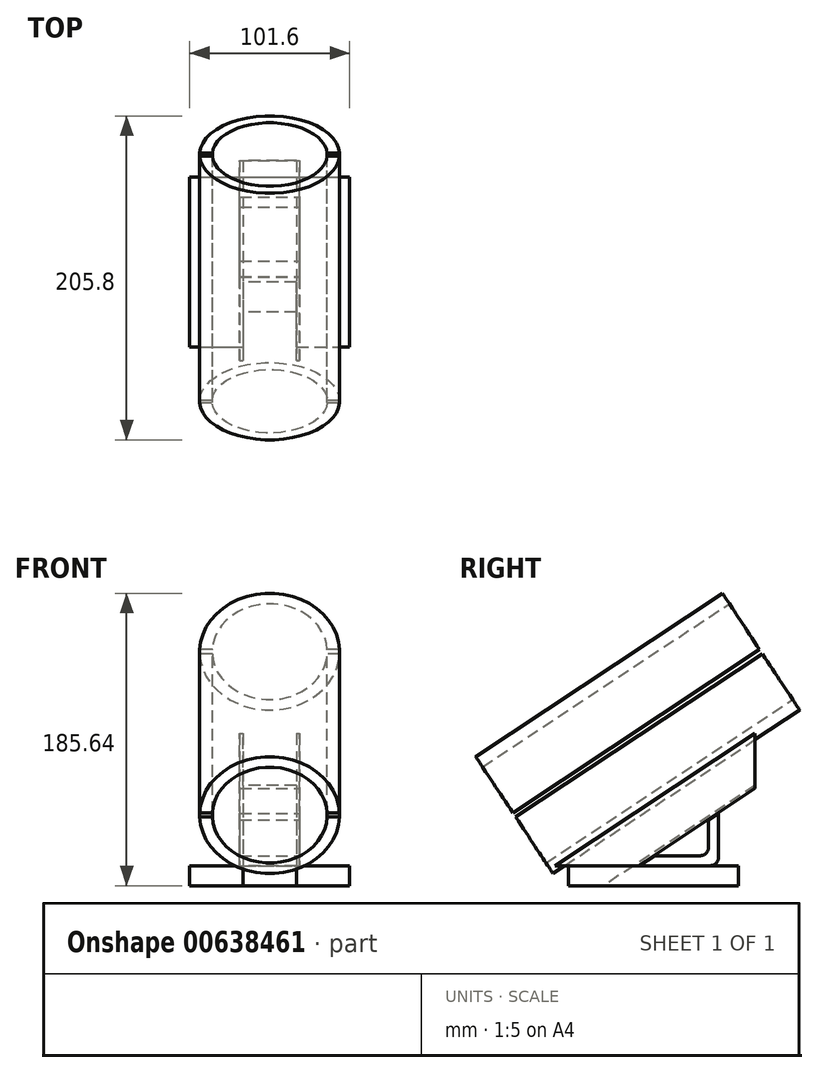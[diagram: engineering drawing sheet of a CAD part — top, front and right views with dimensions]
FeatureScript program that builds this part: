
annotation { "Feature Type Name" : "Feature", "Feature Type Description" : "" }
export const myFeature = defineFeature(function(context is Context, id is Id, definition is map)
    precondition{}
    {
        {
            var Q0;
            Q0=qCreatedBy(makeId("Top.planeOp"),FACE);
            var sketch = newSketch(context, id + "F0", { "sketchPlane" : qUnion([Q0])});
            skLineSegment(sketch, "E0.bottom", {"start": v(-50.8, 53.98) * mm, "end": v(50.8, 53.98) * mm});
            skLineSegment(sketch, "E0.top", {"start": v(-50.8, -53.98) * mm, "end": v(50.8, -53.98) * mm});
            skLineSegment(sketch, "E0.left", {"start": v(-50.8, 53.98) * mm, "end": v(-50.8, -53.98) * mm});
            skLineSegment(sketch, "E0.right", {"start": v(50.8, 53.98) * mm, "end": v(50.8, -53.98) * mm});
            skPoint(sketch, "E0.middle", {"position": v(0, 0) * mm});
            skSolve(sketch);
        }
        {
            var Q0;
            Q0 = qSketchRegion(id + "F0", true);
            extrude(context, id + "F1", {"entities" : qUnion([Q0]), "oppositeDirection" : true, "depth" : 12.7 * mm, "offsetDistance" : 25.4 * mm});
        }
        {
            var Q0;
            Q0=qCreatedBy(makeId("Right.planeOp"),FACE);
            cPlane(context, id + "F2", {"entities" : qUnion([Q0]), "cplaneType" : CPlaneType.OFFSET, "offset" : 19.05 * mm, "width" : 152.4 * mm, "height" : 152.4 * mm});
        }
        {
            var Q0;
            Q0=qCreatedBy(id+"F2.planeOp",FACE);
            var sketch = newSketch(context, id + "F3", { "sketchPlane" : qUnion([Q0])});
            skLineSegment(sketch, "E1", {"start": v(-62.56, 0) * mm, "end": v(64.53, 84.12) * mm});
            skLineSegment(sketch, "E2", {"start": v(64.53, 84.12) * mm, "end": v(64.53, 49.02) * mm});
            skLineSegment(sketch, "E3", {"start": v(64.53, 49.02) * mm, "end": v(-9.53, 0) * mm});
            skLineSegment(sketch, "E4", {"start": v(-9.52, 0) * mm, "end": v(-62.56, 0) * mm});
            skLineSegment(sketch, "E5", {"start": v(0.53, 6.35) * mm, "end": v(34.92, 6.35) * mm});
            skLineSegment(sketch, "E6", {"start": v(34.92, 6.35) * mm, "end": v(34.92, 29.12) * mm});
            skLineSegment(sketch, "E7", {"start": v(34.92, 29.42) * mm, "end": v(41.27, 33.62) * mm});
            skLineSegment(sketch, "E8", {"start": v(41.27, 33.32) * mm, "end": v(41.27, 0) * mm});
            skLineSegment(sketch, "E9", {"start": v(41.27, 0) * mm, "end": v(-9.06, 0) * mm});
            skLineSegment(sketch, "E10", {"start": v(-9.06, 0) * mm, "end": v(0.53, 6.35) * mm});
            skLineSegment(sketch, "E11", {"start": v(34.92, 29.12) * mm, "end": v(41.27, 33.32) * mm});
            skSolve(sketch);
        }
        {
            var Q0;
            Q0 = qSketchRegion(id + "F3", true);
            extrude(context, id + "F4", {"entities" : qUnion([Q0]), "oppositeDirection" : true, "depth" : 38.1 * mm, "offsetDistance" : 25.4 * mm});
        }
        {
            var Q0;
            Q0=makeQuery(id+"F4.opExtrude","SWEPT_FACE",FACE,{"disambiguationData":[OSD([sQuery(id+"F3.wireOp",EDGE,"E2")])]});
            var sketch = newSketch(context, id + "F5", { "sketchPlane" : qUnion([Q0])});
            skLineSegment(sketch, "E12", {"start": v(-17.05, 84.12) * mm, "end": v(-17.05, 51.02) * mm});
            skLineSegment(sketch, "E13", {"start": v(-17.05, 51.02) * mm, "end": v(17.05, 51.02) * mm});
            skLineSegment(sketch, "E14", {"start": v(17.05, 51.02) * mm, "end": v(17.05, 84.12) * mm});
            skLineSegment(sketch, "E15", {"start": v(17.05, 84.12) * mm, "end": v(-17.05, 84.12) * mm});
            skSolve(sketch);
        }
        {
            var Q0;
            Q0=makeQuery(id+"F5.imprint","IMPRINT",FACE,{"disambiguationData":[TD([[makeQuery(id+"F5.imprint","IMPRINT",EDGE,{"derivedFrom":sQuery(id+"F5.wireOp",EDGE,"E12")}),1.0]])]});
            var Q1;
            Q1=makeQuery(id+"F4.opExtrude","CAP_EDGE",EDGE,{"disambiguationData":[OSD([sQuery(id+"F3.wireOp",EDGE,"E1")])],"isStart":true});
            sweep(context, id + "F6", {"operationType" : NewBodyOperationType.REMOVE, "profiles" : qUnion([Q0]), "path" : qUnion([Q1])});
        }
        {
            var Q0;
            Q0=makeQuery(id+"F4.opExtrude","SWEPT_EDGE",EDGE,{"disambiguationData":[OSD([sQuery(id+"F3.wireOp",EDGE,"E8"),sQuery(id+"F3.wireOp",EDGE,"E9")])]});
            var Q1;
            Q1=makeQuery(id+"F4.opExtrude","SWEPT_EDGE",EDGE,{"disambiguationData":[OSD([sQuery(id+"F3.wireOp",EDGE,"E5"),sQuery(id+"F3.wireOp",EDGE,"E6")])]});
            fillet(context, id + "F7", {"entities" : qUnion([Q0, Q1]), "radius" : 5.08 * mm, "tangentPropagation" : true, "allowEdgeOverflow" : false});
        }
        {
            var Q0;
            {var subQ0=sQuery(id+"F3.wireOp",EDGE,"E1");var subQ1=sQuery(id+"F3.wireOp",EDGE,"E2");Q0=makeQuery(id+"F6.boolean.opBoolean","SPLIT",EDGE,{"disambiguationData":[TD([makeQuery(id+"F6.opSweep","SWEPT_FACE",FACE,{"disambiguationData":[OSD([subQ0,sQuery(id+"F5.wireOp",EDGE,"E12")])]})])],"derivedFrom":makeQuery(id+"F4.opExtrude","SWEPT_EDGE",EDGE,{"disambiguationData":[OSD([subQ0,subQ1])]})});}
            cPlane(context, id + "F8", {"entities" : qUnion([Q0]), "cplaneType" : CPlaneType.LINE_ANGLE, "offset" : 25.4 * mm, "angle" : 146.5 * degree, "oppositeDirection" : true, "width" : 152.4 * mm, "height" : 152.4 * mm});
        }
        {
            var Q0;
            Q0=qCreatedBy(id+"F8.planeOp",FACE);
            cPlane(context, id + "F9", {"entities" : qUnion([Q0]), "cplaneType" : CPlaneType.OFFSET, "offset" : 31.75 * mm, "oppositeDirection" : true, "width" : 152.4 * mm, "height" : 152.4 * mm});
        }
        {
            var Q0;
            Q0=qCreatedBy(id+"F9.planeOp",FACE);
            var sketch = newSketch(context, id + "F10", { "sketchPlane" : qUnion([Q0])});
            skCircle(sketch, "E16", {"center": v(0, 75.58) * mm, "radius": 44.45 * mm});
            skCircle(sketch, "E17", {"center": v(0, 75.58) * mm, "radius": 36.51 * mm});
            skSolve(sketch);
        }
        {
            var Q0;
            Q0 = qSketchRegion(id + "F10", true);
            extrude(context, id + "F11", {"entities" : qUnion([Q0]), "operationType" : NewBodyOperationType.ADD, "depth" : 187.96 * mm, "offsetDistance" : 25.4 * mm});
        }
        {
            var Q0;
            Q0=makeQuery(id+"F11.opExtrude","CAP_FACE",FACE,{"disambiguationData":[OSD([sQuery(id+"F10.wireOp",EDGE,"E16"),sQuery(id+"F10.wireOp",EDGE,"E17")])],"isStart":true});
            var sketch = newSketch(context, id + "F12", { "sketchPlane" : qUnion([Q0])});
            skLineSegment(sketch, "E18", {"start": v(0, 75.58) * mm, "end": v(-44.45, 75.58) * mm, "construction": true});
            skLineSegment(sketch, "E19", {"start": v(0, 120.03) * mm, "end": v(0, 75.58) * mm, "construction": true});
            skLineSegment(sketch, "E20", {"start": v(-44.45, 75.58) * mm, "end": v(-44.45, 77.16) * mm});
            skLineSegment(sketch, "E21", {"start": v(-44.45, 77.16) * mm, "end": v(0, 77.16) * mm});
            skLineSegment(sketch, "E22.MirrorCS", {"start": v(44.45, 77.16) * mm, "end": v(0, 77.16) * mm});
            skLineSegment(sketch, "E23.MirrorCS", {"start": v(44.45, 75.58) * mm, "end": v(44.45, 77.16) * mm});
            skLineSegment(sketch, "E24.MirrorCS", {"start": v(-44.45, 75.58) * mm, "end": v(-44.45, 73.99) * mm});
            skLineSegment(sketch, "E25.MirrorCS", {"start": v(-44.45, 73.99) * mm, "end": v(0, 73.99) * mm});
            skLineSegment(sketch, "E26.MirrorCS", {"start": v(44.45, 73.99) * mm, "end": v(0, 73.99) * mm});
            skLineSegment(sketch, "E27.MirrorCS", {"start": v(44.45, 75.58) * mm, "end": v(44.45, 73.99) * mm});
            skSolve(sketch);
        }
        {
            var Q0;
            Q0 = qSketchRegion(id + "F12", true);
            extrude(context, id + "F13", {"entities" : qUnion([Q0]), "operationType" : NewBodyOperationType.REMOVE, "endBound" : BoundingType.THROUGH_ALL, "oppositeDirection" : true, "depth" : 25.4 * mm, "offsetDistance" : 25.4 * mm});
        }
    });
